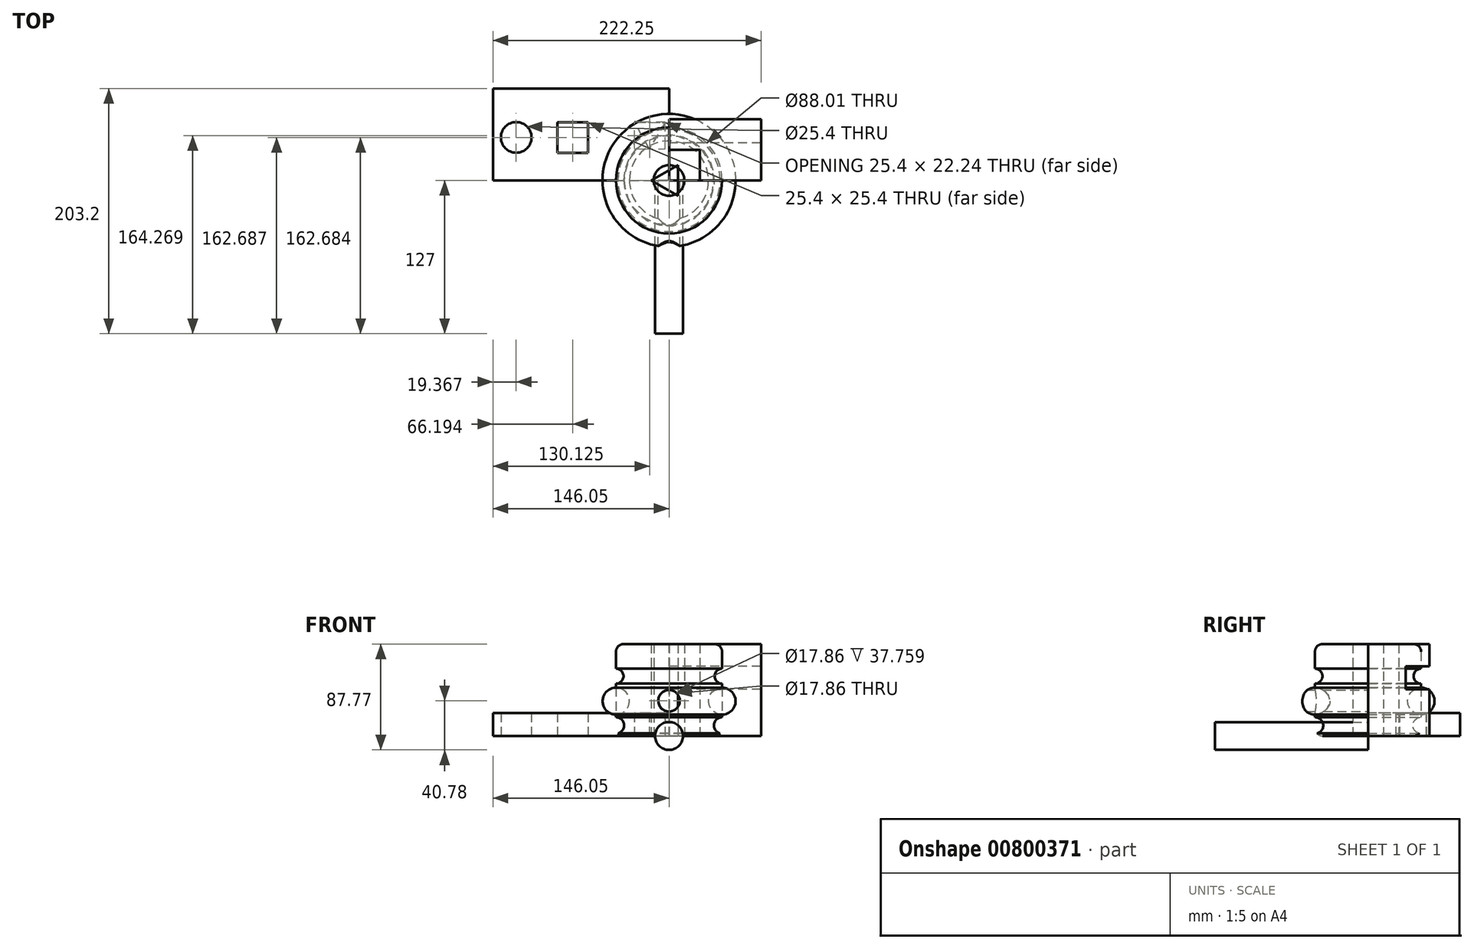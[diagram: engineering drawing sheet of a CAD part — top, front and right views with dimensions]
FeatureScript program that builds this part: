
annotation { "Feature Type Name" : "Feature", "Feature Type Description" : "" }
export const myFeature = defineFeature(function(context is Context, id is Id, definition is map)
    precondition{}
    {
        {
            var Q0;
            Q0=qCreatedBy(makeId("Top.planeOp"),FACE);
            var sketch = newSketch(context, id + "F0", { "sketchPlane" : qUnion([Q0])});
            skCircle(sketch, "E0", {"center": v(0, 0) * mm, "radius": 12.7 * mm});
            skSolve(sketch);
        }
        {
            var Q0;
            Q0=makeQuery(id+"F0.imprint","IMPRINT",FACE,{"disambiguationData":[TD([[makeQuery(id+"F0.imprint","IMPRINT",EDGE,{"derivedFrom":sQuery(id+"F0.wireOp",EDGE,"E0")}),1.0]])]});
            extrude(context, id + "F1", {"entities" : qUnion([Q0]), "depth" : 76.2 * mm, "offsetDistance" : 25.4 * mm});
        }
        {
            var Q0;
            Q0=qCreatedBy(makeId("Top.planeOp"),FACE);
            var sketch = newSketch(context, id + "F2", { "sketchPlane" : qUnion([Q0])});
            skLineSegment(sketch, "E1.bottom", {"start": v(0, 0) * mm, "end": v(25.4, 0) * mm});
            skLineSegment(sketch, "E1.top", {"start": v(0, 25.4) * mm, "end": v(25.4, 25.4) * mm});
            skLineSegment(sketch, "E1.left", {"start": v(0, 0) * mm, "end": v(0, 25.4) * mm});
            skLineSegment(sketch, "E1.right", {"start": v(25.4, 0) * mm, "end": v(25.4, 25.4) * mm});
            skSolve(sketch);
        }
        {
            var Q0;
            Q0=makeQuery(id+"F2.imprint","IMPRINT",FACE,{"disambiguationData":[TD([[makeQuery(id+"F2.imprint","IMPRINT",EDGE,{"derivedFrom":sQuery(id+"F2.wireOp",EDGE,"E1.bottom")}),1.0]])]});
            extrude(context, id + "F3", {"entities" : qUnion([Q0]), "depth" : 76.2 * mm, "offsetDistance" : 25.4 * mm});
        }
        {
            var Q0;
            Q0=qCreatedBy(makeId("Top.planeOp"),FACE);
            var sketch = newSketch(context, id + "F4", { "sketchPlane" : qUnion([Q0])});
            skCircle(sketch, "E2.cCircle", {"center": v(0, 0) * mm, "radius": 7.33 * mm, "construction": true});
            skLineSegment(sketch, "E2.0", {"start": v(7.33, 12.7) * mm, "end": v(7.33, -12.7) * mm});
            skLineSegment(sketch, "E2.1", {"start": v(7.33, -12.7) * mm, "end": v(-14.66, 0) * mm});
            skLineSegment(sketch, "E2.2", {"start": v(-14.66, 0) * mm, "end": v(7.33, 12.7) * mm});
            skPoint(sketch, "E2.0.midPoint", {"position": v(7.33, 0) * mm});
            skSolve(sketch);
        }
        {
            var Q0;
            Q0=makeQuery(id+"F4.imprint","IMPRINT",FACE,{"disambiguationData":[TD([[makeQuery(id+"F4.imprint","IMPRINT",EDGE,{"derivedFrom":sQuery(id+"F4.wireOp",EDGE,"E2.0")}),-1.0]])]});
            extrude(context, id + "F5", {"entities" : qUnion([Q0]), "depth" : 76.2 * mm, "offsetDistance" : 25.4 * mm});
        }
        {
            var Q0;
            Q0=qCreatedBy(makeId("Top.planeOp"),FACE);
            var sketch = newSketch(context, id + "F6", { "sketchPlane" : qUnion([Q0])});
            skLineSegment(sketch, "E3.bottom", {"start": v(-146.05, 76.2) * mm, "end": v(0, 76.2) * mm});
            skLineSegment(sketch, "E3.top", {"start": v(-146.05, 0) * mm, "end": v(0, 0) * mm});
            skLineSegment(sketch, "E3.left", {"start": v(-146.05, 76.2) * mm, "end": v(-146.05, 0) * mm});
            skLineSegment(sketch, "E3.right", {"start": v(0, 76.2) * mm, "end": v(0, 0) * mm});
            skCircle(sketch, "E4", {"center": v(-126.68, 35.69) * mm, "radius": 12.7 * mm});
            skLineSegment(sketch, "E5.bottom", {"start": v(-92.56, 48.38) * mm, "end": v(-67.16, 48.38) * mm});
            skLineSegment(sketch, "E5.top", {"start": v(-92.56, 22.98) * mm, "end": v(-67.16, 22.98) * mm});
            skLineSegment(sketch, "E5.left", {"start": v(-92.56, 48.38) * mm, "end": v(-92.56, 22.98) * mm});
            skLineSegment(sketch, "E5.right", {"start": v(-67.16, 48.38) * mm, "end": v(-67.16, 22.98) * mm});
            skCircle(sketch, "E6.cCircle", {"center": v(-16.07, 40.81) * mm, "radius": 7.33 * mm, "construction": true});
            skLineSegment(sketch, "E6.0", {"start": v(-3.23, 47.9) * mm, "end": v(-16.35, 26.15) * mm});
            skLineSegment(sketch, "E6.1", {"start": v(-16.35, 26.15) * mm, "end": v(-28.62, 48.39) * mm});
            skLineSegment(sketch, "E6.2", {"start": v(-28.62, 48.39) * mm, "end": v(-3.23, 47.9) * mm});
            skPoint(sketch, "E6.0.midPoint", {"position": v(-9.79, 37.03) * mm});
            skSolve(sketch);
        }
        {
            var Q0;
            Q0=makeQuery(id+"F6.imprint","IMPRINT",FACE,{"disambiguationData":[TD([[makeQuery(id+"F6.imprint","IMPRINT",EDGE,{"derivedFrom":sQuery(id+"F6.wireOp",EDGE,"E3.bottom")}),-1.0]])]});
            extrude(context, id + "F7", {"entities" : qUnion([Q0]), "depth" : 19.05 * mm, "offsetDistance" : 25.4 * mm});
        }
        {
            var Q0;
            Q0=qCreatedBy(makeId("Right.planeOp"),FACE);
            var sketch = newSketch(context, id + "F8", { "sketchPlane" : qUnion([Q0])});
            skLineSegment(sketch, "E7.bottom", {"start": v(0, 0) * mm, "end": v(50.8, 0) * mm});
            skLineSegment(sketch, "E7.top", {"start": v(0, 76.2) * mm, "end": v(50.8, 76.2) * mm});
            skLineSegment(sketch, "E7.left", {"start": v(0, 0) * mm, "end": v(0, 76.2) * mm});
            skLineSegment(sketch, "E7.right", {"start": v(50.8, 0) * mm, "end": v(50.8, 76.2) * mm});
            skLineSegment(sketch, "E8.bottom", {"start": v(50.8, 57.63) * mm, "end": v(31.24, 57.63) * mm});
            skLineSegment(sketch, "E8.top", {"start": v(50.8, 38.58) * mm, "end": v(31.24, 38.58) * mm});
            skLineSegment(sketch, "E8.left", {"start": v(50.8, 57.63) * mm, "end": v(50.8, 38.58) * mm});
            skLineSegment(sketch, "E8.right", {"start": v(31.24, 57.63) * mm, "end": v(31.24, 38.58) * mm});
            skSolve(sketch);
        }
        {
            var Q0;
            {var subQ1=sQuery(id+"F8.wireOp",EDGE,"E7.bottom");Q0=makeQuery(id+"F8.imprint","IMPRINT",FACE,{"disambiguationData":[TD([[makeQuery(id+"F8.imprint","IMPRINT",EDGE,{"derivedFrom":subQ1}),1.0]])]});}
            extrude(context, id + "F9", {"entities" : qUnion([Q0]), "depth" : 76.2 * mm, "offsetDistance" : 25.4 * mm});
        }
        {
            var Q0;
            Q0=qCreatedBy(makeId("Front.planeOp"),FACE);
            var sketch = newSketch(context, id + "F10", { "sketchPlane" : qUnion([Q0])});
            skLineSegment(sketch, "E9.bottom", {"start": v(0, 0) * mm, "end": v(37.66, 0) * mm});
            skLineSegment(sketch, "E9.top", {"start": v(0, 76.2) * mm, "end": v(37.66, 76.2) * mm});
            skLineSegment(sketch, "E9.left", {"start": v(0, 0) * mm, "end": v(0, 76.2) * mm});
            skLineSegment(sketch, "E9.right", {"start": v(44, 6.35) * mm, "end": v(44, 69.85) * mm});
            skCircle(sketch, "E10", {"center": v(44, 49.64) * mm, "radius": 6.23 * mm});
            skCircle(sketch, "E11", {"center": v(44, 28.9) * mm, "radius": 11.16 * mm});
            skCircle(sketch, "E12", {"center": v(44, 8.74) * mm, "radius": 6.84 * mm});
            skPoint(sketch, "E13.visualSharp", {"position": v(44, 76.2) * mm});
            skArc(sketch, "E13.filletArc", {"start": v(44, 69.85) * mm, "mid": v(42.15, 74.34) * mm, "end": v(37.66, 76.2) * mm});
            skPoint(sketch, "E14.visualSharp", {"position": v(44, 0) * mm});
            skArc(sketch, "E14.filletArc", {"start": v(37.66, 0) * mm, "mid": v(42.15, 1.86) * mm, "end": v(44, 6.35) * mm});
            skSolve(sketch);
        }
        {
            var Q0;
            {var subQ8=sQuery(id+"F10.wireOp",EDGE,"E9.bottom");Q0=makeQuery(id+"F10.imprint","IMPRINT",FACE,{"disambiguationData":[TD([[makeQuery(id+"F10.imprint","IMPRINT",EDGE,{"derivedFrom":subQ8}),1.0]])]});}
            var Q1;
            {var subQ0=sQuery(id+"F10.wireOp",EDGE,"E11");var subQ1=sQuery(id+"F10.wireOp",EDGE,"E9.right");var subQ2=makeQuery(id+"F10.imprint","INTERSECT",VERTEX,{"disambiguationData":[OD(0.0)],"derivedFrom":[subQ1,subQ0]});Q1=makeQuery(id+"F10.imprint","IMPRINT",FACE,{"disambiguationData":[TD([[makeQuery(id+"F10.imprint","IMPRINT",EDGE,{"disambiguationData":[TD([[subQ2,-1.0]])],"derivedFrom":subQ1}),-1.0]])]});}
            var Q2;
            Q2=sQuery(id+"F10.wireOp",EDGE,"E9.left");
            revolve(context, id + "F11", {"surfaceOperationType" : NewSurfaceOperationType.NEW, "entities" : qUnion([Q0, Q1]), "axis" : qUnion([Q2]), "revolveType" : RevolveType.FULL});
        }
        {
            var Q0;
            Q0=qCreatedBy(makeId("Front.planeOp"),FACE);
            var sketch = newSketch(context, id + "F12", { "sketchPlane" : qUnion([Q0])});
            skPoint(sketch, "E15", {"position": v(0, 29.21) * mm});
            skSolve(sketch);
        }
        {
            var Q0;
            Q0=sQuery(id+"F12.wireOp",VERTEX,"E15");
            var Q1;
            Q1=makeQuery(id+"F11.opRevolve","SWEPT_BODY",BODY,{"disambiguationData":[OSD([sQuery(id+"F10.wireOp",EDGE,"E9.bottom"),sQuery(id+"F10.wireOp",EDGE,"E9.top"),sQuery(id+"F10.wireOp",EDGE,"E9.left"),sQuery(id+"F10.wireOp",EDGE,"E9.right"),sQuery(id+"F10.wireOp",EDGE,"E10"),sQuery(id+"F10.wireOp",EDGE,"E11"),sQuery(id+"F10.wireOp",EDGE,"E12"),sQuery(id+"F10.wireOp",EDGE,"E13.filletArc"),sQuery(id+"F10.wireOp",EDGE,"E14.filletArc")])]});
            var Q2;
            Q2=makeQuery(id+"F11.opRevolve","SWEPT_BODY",BODY,{"disambiguationData":[OSD([sQuery(id+"F10.wireOp",EDGE,"E9.right"),sQuery(id+"F10.wireOp",EDGE,"E11")])]});
            hole(context, id + "F13", {"style" : HoleStyle.SIMPLE, "endStyle" : HoleEndStyle.THROUGH, "oppositeDirection" : true, "standardTappedOrClearance" : lookupTablePath({ "standard" : "ANSI", "engagement" : "75%", "pitch" : "20 tpi", "size" : "3/4", "type" : "Tapped" }), "standardBlindInLast" : lookupTablePath({ "standard" : "ANSI", "engagement" : "75%", "pitch" : "20 tpi", "size" : "3/4", "type" : "Tapped" }), "holeDiameter" : 17.86 * mm, "majorDiameter" : 19.05 * mm, "showTappedDepth" : true, "isTappedThrough" : true, "tappedDepth" : 12.7 * mm, "tapClearance" : 3, "locations" : qUnion([Q0]), "scope" : qUnion([Q1, Q2])});
        }
        {
            var Q0;
            Q0=qCreatedBy(makeId("Front.planeOp"),FACE);
            var sketch = newSketch(context, id + "F14", { "sketchPlane" : qUnion([Q0])});
            skCircle(sketch, "E16", {"center": v(0, 0) * mm, "radius": 11.57 * mm});
            skSolve(sketch);
        }
        {
            var Q0;
            Q0=makeQuery(id+"F14.imprint","IMPRINT",FACE,{"disambiguationData":[TD([[makeQuery(id+"F14.imprint","IMPRINT",EDGE,{"derivedFrom":sQuery(id+"F14.wireOp",EDGE,"E16")}),1.0]])]});
            extrude(context, id + "F15", {"entities" : qUnion([Q0]), "depth" : 127 * mm, "offsetDistance" : 25.4 * mm});
        }
    });
